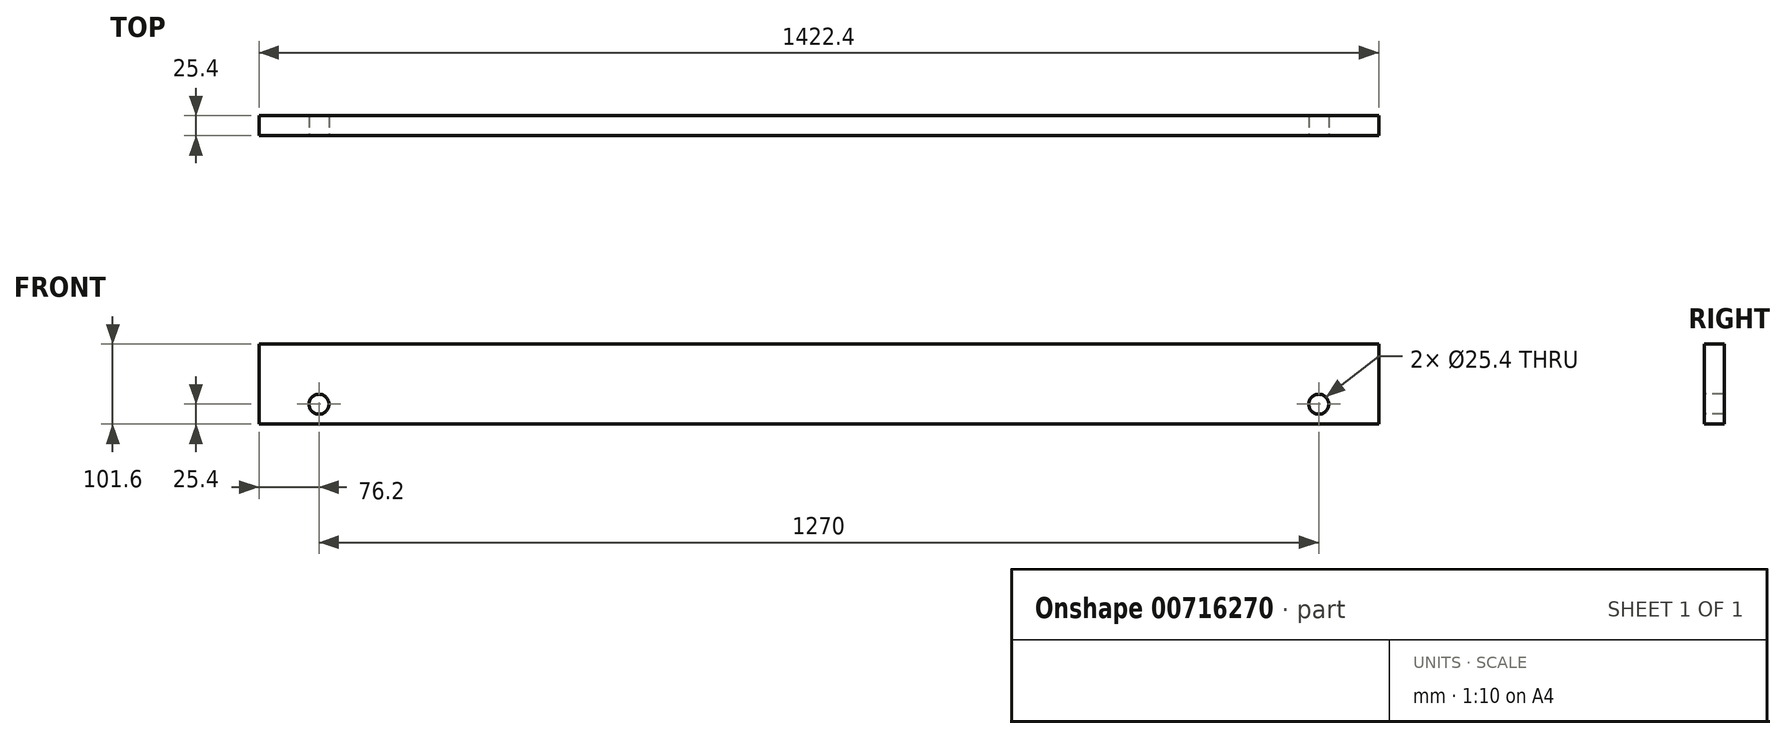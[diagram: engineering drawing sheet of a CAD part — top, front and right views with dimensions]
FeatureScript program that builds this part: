
annotation { "Feature Type Name" : "Feature", "Feature Type Description" : "" }
export const myFeature = defineFeature(function(context is Context, id is Id, definition is map)
    precondition{}
    {
        {
            var Q0;
            Q0=qCreatedBy(makeId("Front.planeOp"),FACE);
            var sketch = newSketch(context, id + "F0", { "sketchPlane" : qUnion([Q0])});
            skLineSegment(sketch, "E0.bottom", {"start": v(0, 101.6) * mm, "end": v(1422.4, 101.6) * mm});
            skLineSegment(sketch, "E0.top", {"start": v(0, 0) * mm, "end": v(1422.4, 0) * mm});
            skLineSegment(sketch, "E0.left", {"start": v(0, 101.6) * mm, "end": v(0, 0) * mm});
            skLineSegment(sketch, "E0.right", {"start": v(1422.4, 101.6) * mm, "end": v(1422.4, 0) * mm});
            skSolve(sketch);
        }
        {
            var Q0;
            Q0=makeQuery(id+"F0.imprint","IMPRINT",FACE,{"disambiguationData":[TD([[makeQuery(id+"F0.imprint","IMPRINT",EDGE,{"derivedFrom":sQuery(id+"F0.wireOp",EDGE,"E0.bottom")}),-1.0]])]});
            extrude(context, id + "F1", {"entities" : qUnion([Q0]), "depth" : 25.4 * mm, "offsetDistance" : 25.4 * mm});
        }
        {
            var Q0;
            Q0=makeQuery(id+"F1.opExtrude","CAP_FACE",FACE,{"disambiguationData":[OSD([sQuery(id+"F0.wireOp",EDGE,"E0.bottom"),sQuery(id+"F0.wireOp",EDGE,"E0.top"),sQuery(id+"F0.wireOp",EDGE,"E0.left"),sQuery(id+"F0.wireOp",EDGE,"E0.right")])],"isStart":false});
            var sketch = newSketch(context, id + "F2", { "sketchPlane" : qUnion([Q0])});
            skLineSegment(sketch, "E1", {"start": v(0, 50.8) * mm, "end": v(76.2, 50.8) * mm, "construction": true});
            skLineSegment(sketch, "E2", {"start": v(1422.4, 50.8) * mm, "end": v(1346.2, 50.8) * mm, "construction": true});
            skLineSegment(sketch, "E3", {"start": v(76.2, 101.6) * mm, "end": v(76.2, 50.8) * mm});
            skLineSegment(sketch, "E4", {"start": v(76.2, 50.8) * mm, "end": v(76.2, 0) * mm});
            skPoint(sketch, "E5", {"position": v(76.2, 25.4) * mm});
            skPoint(sketch, "E6", {"position": v(76.2, 76.2) * mm});
            skLineSegment(sketch, "E7", {"start": v(1346.2, 101.6) * mm, "end": v(1346.2, 50.8) * mm});
            skLineSegment(sketch, "E8", {"start": v(1346.2, 50.8) * mm, "end": v(1346.2, 0) * mm});
            skPoint(sketch, "E9", {"position": v(1346.2, 25.4) * mm});
            skPoint(sketch, "E10", {"position": v(1346.2, 76.2) * mm});
            skCircle(sketch, "E11", {"center": v(1346.2, 25.4) * mm, "radius": 12.7 * mm});
            skCircle(sketch, "E12", {"center": v(76.2, 25.4) * mm, "radius": 12.7 * mm});
            skSolve(sketch);
        }
        {
            var Q0;
            Q0=qSketchRegion(id+"F2",true);
            extrude(context, id + "F3", {"entities" : qUnion([Q0]), "operationType" : NewBodyOperationType.REMOVE, "endBound" : BoundingType.THROUGH_ALL, "oppositeDirection" : true, "depth" : 25.4 * mm, "offsetDistance" : 25.4 * mm});
        }
    });
